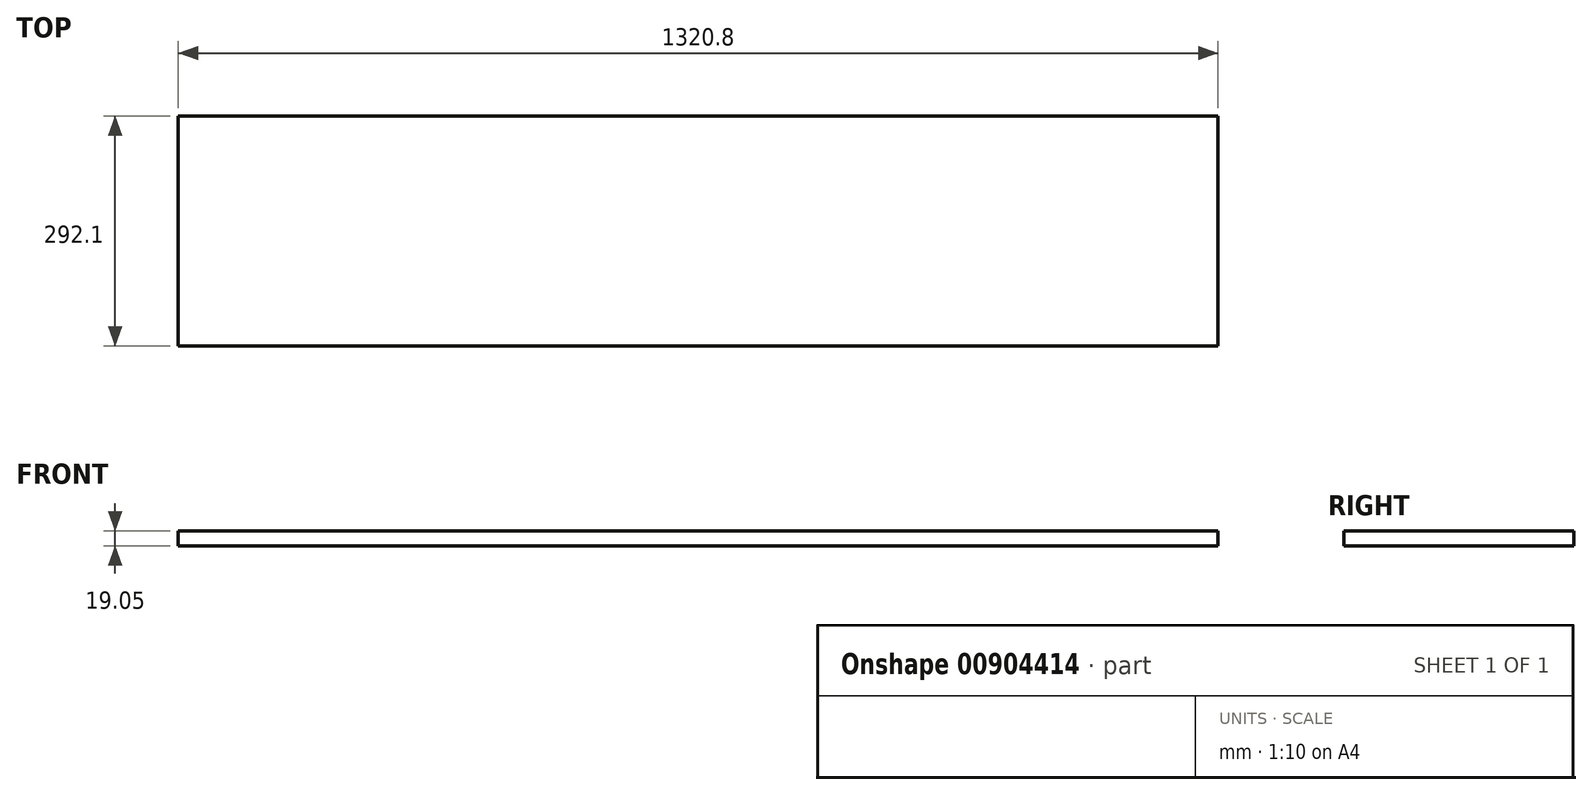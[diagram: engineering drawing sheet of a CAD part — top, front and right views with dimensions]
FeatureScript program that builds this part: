
annotation { "Feature Type Name" : "Feature", "Feature Type Description" : "" }
export const myFeature = defineFeature(function(context is Context, id is Id, definition is map)
    precondition{}
    {
        {
            var Q0;
            Q0=qCreatedBy(makeId("Top.planeOp"),FACE);
            var sketch = newSketch(context, id + "F0", { "sketchPlane" : qUnion([Q0])});
            skLineSegment(sketch, "E0.bottom", {"start": v(0, 0) * mm, "end": v(1320.8, 0) * mm});
            skLineSegment(sketch, "E0.top", {"start": v(0, 292.1) * mm, "end": v(1320.8, 292.1) * mm});
            skLineSegment(sketch, "E0.left", {"start": v(0, 0) * mm, "end": v(0, 292.1) * mm});
            skLineSegment(sketch, "E0.right", {"start": v(1320.8, 0) * mm, "end": v(1320.8, 292.1) * mm});
            skSolve(sketch);
        }
        {
            var Q0;
            Q0 = qSketchRegion(id + "F0", true);
            extrude(context, id + "F1", {"entities" : qUnion([Q0]), "depth" : 19.05 * mm, "offsetDistance" : 25.4 * mm});
        }
    });
